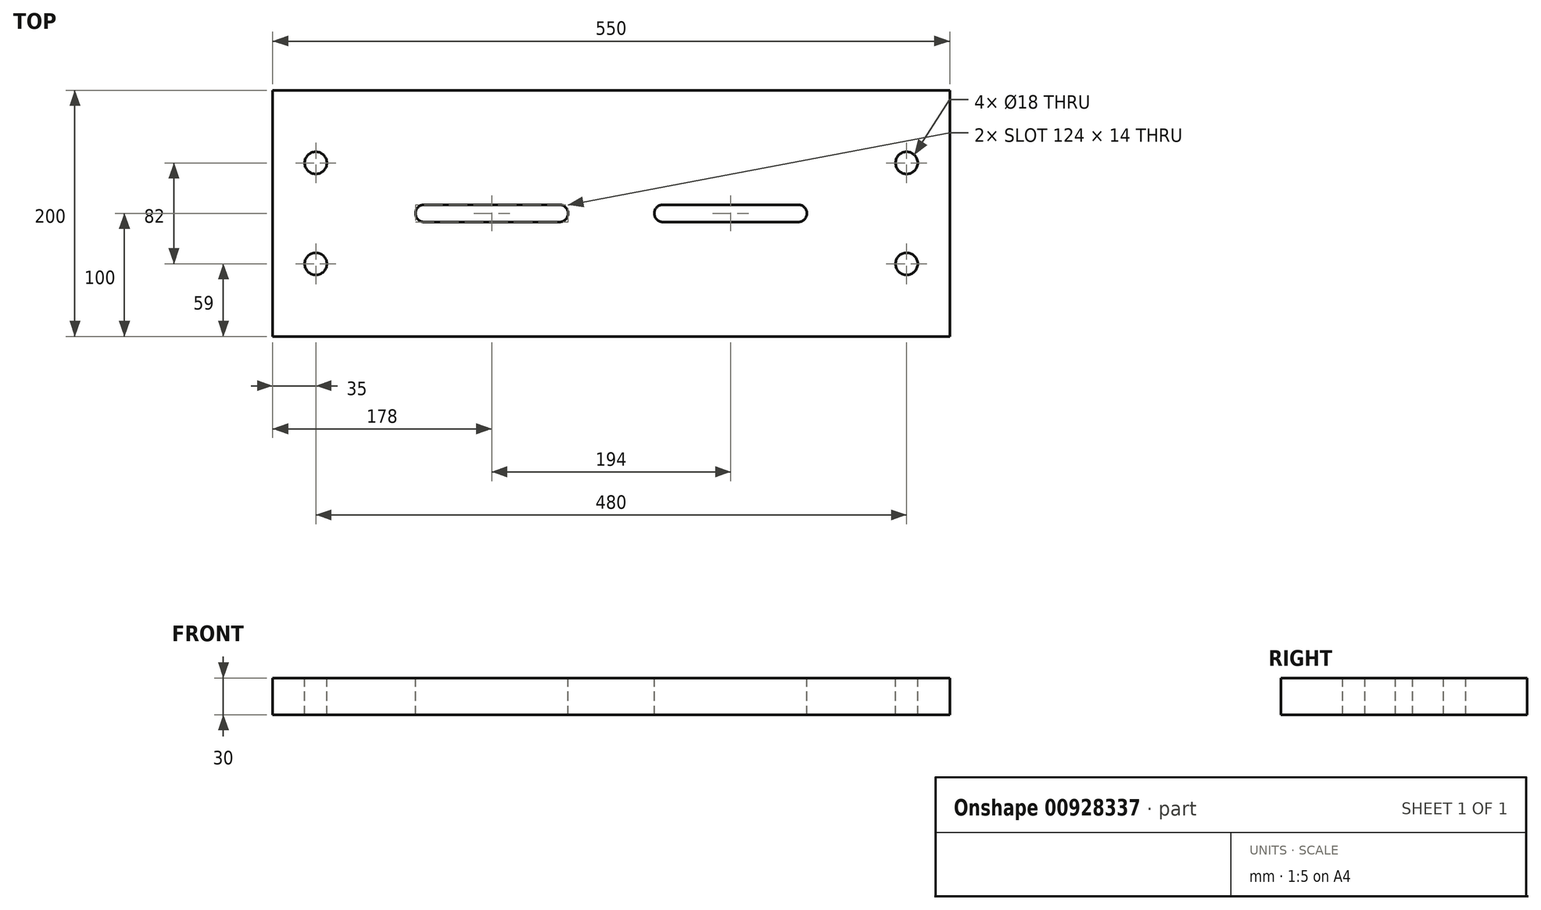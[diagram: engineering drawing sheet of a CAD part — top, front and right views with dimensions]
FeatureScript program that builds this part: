
annotation { "Feature Type Name" : "Feature", "Feature Type Description" : "" }
export const myFeature = defineFeature(function(context is Context, id is Id, definition is map)
    precondition{}
    {
        {
            var Q0;
            Q0=qCreatedBy(makeId("Top.planeOp"),FACE);
            var sketch = newSketch(context, id + "F0", { "sketchPlane" : qUnion([Q0])});
            skLineSegment(sketch, "E0.bottom", {"start": v(275, 100) * mm, "end": v(-275, 100) * mm});
            skLineSegment(sketch, "E0.top", {"start": v(275, -100) * mm, "end": v(-275, -100) * mm});
            skLineSegment(sketch, "E0.left", {"start": v(275, 100) * mm, "end": v(275, -100) * mm});
            skLineSegment(sketch, "E0.right", {"start": v(-275, 100) * mm, "end": v(-275, -100) * mm});
            skPoint(sketch, "E0.middle", {"position": v(0, 0) * mm});
            skCircle(sketch, "E1", {"center": v(-240, 41) * mm, "radius": 9 * mm});
            skCircle(sketch, "E2.MirrorC", {"center": v(-240, -41) * mm, "radius": 9 * mm});
            skCircle(sketch, "E3.MirrorC", {"center": v(240, 41) * mm, "radius": 9 * mm});
            skCircle(sketch, "E4.MirrorC", {"center": v(240, -41) * mm, "radius": 9 * mm});
            skLineSegment(sketch, "E5", {"start": v(92, -67.22) * mm, "end": v(92, 57.1) * mm, "construction": true});
            skLineSegment(sketch, "E6", {"start": v(42, 7) * mm, "end": v(152, 7) * mm});
            skLineSegment(sketch, "E7.MirrorCS", {"start": v(42, -7) * mm, "end": v(152, -7) * mm});
            skLineSegment(sketch, "E8", {"start": v(42, 7) * mm, "end": v(42, -7) * mm, "construction": true});
            skLineSegment(sketch, "E9", {"start": v(42, 0) * mm, "end": v(35, 0) * mm, "construction": true});
            skArc(sketch, "E10", {"start": v(42, 7) * mm, "mid": v(35, 0) * mm, "end": v(42, -7) * mm});
            skArc(sketch, "E11.MirrorCS", {"start": v(152, 7) * mm, "mid": v(159, 0) * mm, "end": v(152, -7) * mm});
            skLineSegment(sketch, "E12.MirrorCS", {"start": v(-42, 0) * mm, "end": v(-35, 0) * mm, "construction": true});
            skLineSegment(sketch, "E13.MirrorCS", {"start": v(-42, 7) * mm, "end": v(-42, -7) * mm, "construction": true});
            skLineSegment(sketch, "E14.MirrorCS", {"start": v(-42, -7) * mm, "end": v(-152, -7) * mm});
            skLineSegment(sketch, "E15.MirrorCS", {"start": v(-42, 7) * mm, "end": v(-152, 7) * mm});
            skArc(sketch, "E16.MirrorCS", {"start": v(-42, 7) * mm, "mid": v(-35, 0) * mm, "end": v(-42, -7) * mm});
            skArc(sketch, "E17.MirrorCS", {"start": v(-152, 7) * mm, "mid": v(-159, 0) * mm, "end": v(-152, -7) * mm});
            skSolve(sketch);
        }
        {
            var Q0;
            Q0 = qSketchRegion(id + "F0", true);
            extrude(context, id + "F1", {"entities" : qUnion([Q0]), "depth" : -30 * mm, "offsetDistance" : 25 * mm});
        }
    });
